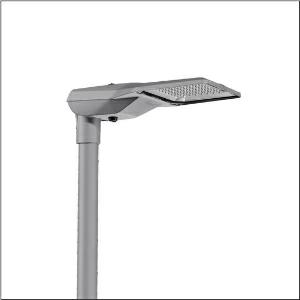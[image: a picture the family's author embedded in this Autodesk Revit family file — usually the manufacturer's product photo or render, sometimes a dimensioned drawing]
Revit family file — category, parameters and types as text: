
# Revit family: streetlight_sl_21_midi___st0_8a_5xe3c63t08nb_b211
name_source: partatom
category: Lighting Fixtures
units: mm (PartAtom-declared; Revit-internal decimal feet)

## family parameters
Cut with Voids When Loaded = No
Host = Face
Light Source = No
Part Type = Normal
Room Calculation Point = No
Round Connector Dimension = Use Diameter
Shared = No

## types (1)
- --- (1 x LED, 20350 lm, 151.2 W, 2700K)
    Apparent Load = 151 VA
    CIE Flux Codes = 41 75 97 100 100
    Color Rendering = 70
    Color Temperature = 2700K
    Default Elevation = 1800 mm
    Description = Streetlight SL 21 midi, mast luminaire, primary light control with lens, of PMMA, primary optical cover: cover, of toughened safety glass, transparent, light distribution: ST0.8a, light emission: direct distribution, primary light characteristic: asymmetric, installation type: side-entry, post-top, LED, High Power LED, rated luminous flux: 20.350lm, luminous efficacy: 135lm/W, light colour: 727, colour temperature: 2700K, control: overheat protection, constant luminous flux control, time-dependent luminous flux control, flexible luminous flux parameterisation, presetting dimming logarithmic, mains connection: 230..240V, AC, 50/60Hz, start of lifetime: 151W, end of service life: 157W, reduction: 70W, luminaire housing, of diecast aluminium, powder-coated, Siteco® metallic grey (DB 702S), corrosivity category C5 mid according to DIN EN ISO 12944, please order mast flange separately, inclination adjustable: 0°, 5°, 10°, 15°, sealing non-destructively replaceable, multi-level sealing system, length: 644mm, width: 335mm, height: 110mm, mast flange for spigot size: 42mm (side-entry): 5XC10008XM4, 60/48mm (side-entry/post-top): 5XC10108XM2, 76/60mm (side-entry/post-top): 5XC10108XM1, Smart Interface below and above, protection rating (complete): IP66, insulation class (complete): insulation class II (safety insulation), certification: CE, ENEC, ENEC+, VDE, impact resistance: IK09, permissible operating ambient temperature for outdoor applications: -40..+50°C, standard-compliant lighting for roads and squares, packaging unit: 1 piece

Light Distribution: ST0.8a
    Height = 111 mm
    Lamp = 1 x LED
    Lamp Light Flux = 20350 lm
    Lamp Power = 151.2 W
    Lamp count = 1
    Length = 644 mm
    Luminous efficacy = 135 lm/W
    Manufacturer = Siteco
    ModVariant = No
    Model = 5XE3C63T08NB
    Number of Poles = 1
    OnlyDefault = Yes
    Power Factor = 1
    Product Name = Streetlight SL 21 midi | ST0.8a
    Product group = mast luminaire | pylon top
    ProductGroupID = 6100
    Protection Class = Protection class II
    Protection Degree = IP 66
    RLX_Detail_Level = 1
    RLX_Emergency_Light_Flux = 0 lm
    RLX_Emergency_Type = 0
    RLX_Emergency_Type_DB = No
    RlxData = <blob elided: 90589 chars, md5=1e68aa0a>
    Socket = socket
    Standby Power = 0 W
    System Light Flux = 20350 lm
    System Power = 151 W
    Type Comments = factory setting: luminous flux: 100 % | dim-lin: 254 | 802 mA
    Type Image = l_1004304.jpg
    URL = http://relux.com
    VarID = @adj_118849
    Voltage = 0 V
    Weight = 0.00 kg
    Width = 336 mm

## geometry (parser evidence)
native form markers: Blend x4, Sweep x11
no freeform markers — native parametric forms only
